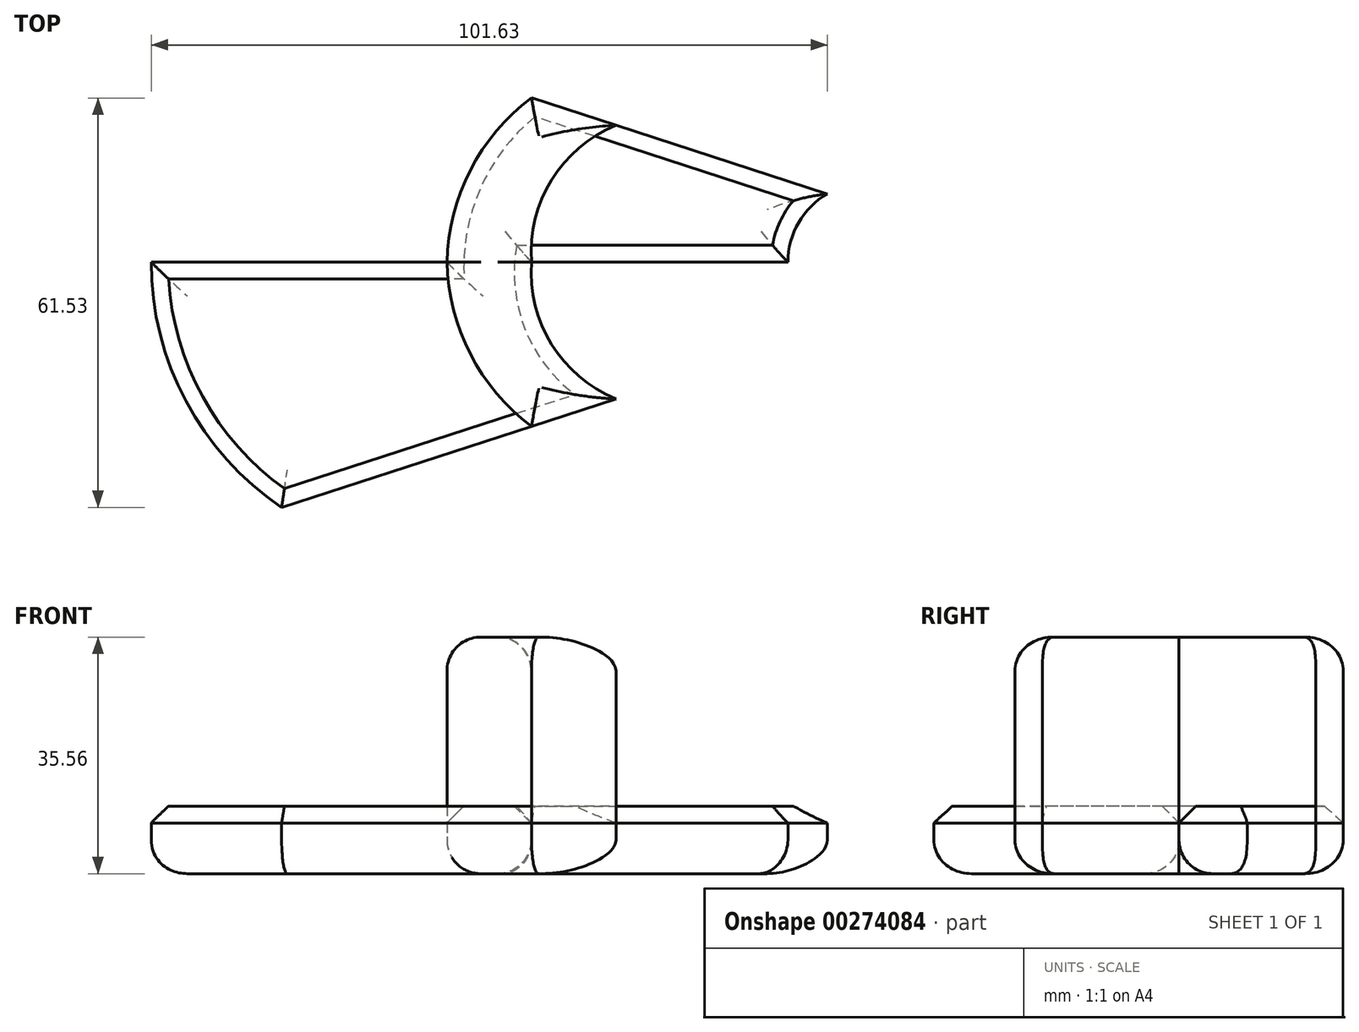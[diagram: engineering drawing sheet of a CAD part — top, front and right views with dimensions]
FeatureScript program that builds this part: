
annotation { "Feature Type Name" : "Feature", "Feature Type Description" : "" }
export const myFeature = defineFeature(function(context is Context, id is Id, definition is map)
    precondition{}
    {
        {
            var Q0;
            Q0=qCreatedBy(makeId("Top.planeOp"),FACE);
            var sketch = newSketch(context, id + "F0", { "sketchPlane" : qUnion([Q0])});
            skLineSegment(sketch, "E0", {"start": v(-50.8, 0) * mm, "end": v(-6.35, 0) * mm});
            skLineSegment(sketch, "E1.MirrorCS", {"start": v(50.8, 0) * mm, "end": v(6.37, 0) * mm});
            skArc(sketch, "E2", {"start": v(-50.8, 0) * mm, "mid": v(-45.6, 20.88) * mm, "end": v(-31.19, 36.86) * mm});
            skArc(sketch, "E3.MirrorCS", {"start": v(-50.8, 0) * mm, "mid": v(-45.6, -20.88) * mm, "end": v(-31.19, -36.86) * mm});
            skLineSegment(sketch, "E4", {"start": v(-31.19, 36.86) * mm, "end": v(50.83, 10.25) * mm});
            skLineSegment(sketch, "E5", {"start": v(50.83, -10.25) * mm, "end": v(-31.19, -36.86) * mm});
            skArc(sketch, "E6", {"start": v(50.83, 10.25) * mm, "mid": v(44.9, 0) * mm, "end": v(50.83, -10.25) * mm});
            skArc(sketch, "E7", {"start": v(6.37, 24.67) * mm, "mid": v(-2.83, 13.8) * mm, "end": v(-6.35, 0) * mm});
            skArc(sketch, "E8.MirrorCS", {"start": v(6.37, -24.67) * mm, "mid": v(-2.83, -13.8) * mm, "end": v(-6.35, 0) * mm});
            skLineSegment(sketch, "E9", {"start": v(6.37, 24.67) * mm, "end": v(19.07, 24.67) * mm});
            skArc(sketch, "E10", {"start": v(19.07, 20.55) * mm, "mid": v(9.36, 12.35) * mm, "end": v(6.37, 0) * mm});
            skArc(sketch, "E11.MirrorCS", {"start": v(19.07, -20.55) * mm, "mid": v(9.36, -12.35) * mm, "end": v(6.37, 0) * mm});
            skSolve(sketch);
        }
        {
            var Q0;
            {var subQ0=sQuery(id+"F0.wireOp",EDGE,"E10");Q0=makeQuery(id+"F0.imprint","IMPRINT",FACE,{"disambiguationData":[TD([[makeQuery(id+"F0.imprint","IMPRINT",EDGE,{"derivedFrom":subQ0}),1.0]])]});}
            var Q1;
            {var subQ0=sQuery(id+"F0.wireOp",EDGE,"E11.MirrorCS");Q1=makeQuery(id+"F0.imprint","IMPRINT",FACE,{"disambiguationData":[TD([[makeQuery(id+"F0.imprint","IMPRINT",EDGE,{"derivedFrom":subQ0}),-1.0]])]});}
            var Q2;
            {var subQ0=sQuery(id+"F0.wireOp",EDGE,"E2");Q2=makeQuery(id+"F0.imprint","IMPRINT",FACE,{"disambiguationData":[TD([[makeQuery(id+"F0.imprint","IMPRINT",EDGE,{"derivedFrom":subQ0}),-1.0]])]});}
            var Q3;
            Q3=makeQuery(id+"F0.imprint","IMPRINT",FACE,{"disambiguationData":[TD([[makeQuery(id+"F0.imprint","IMPRINT",EDGE,{"derivedFrom":sQuery(id+"F0.wireOp",EDGE,"E0")}),-1.0]])]});
            extrude(context, id + "F1", {"entities" : qUnion([Q0, Q1, Q2, Q3]), "depth" : 10.16 * mm});
        }
        {
            var Q0;
            {var subQ1=sQuery(id+"F0.wireOp",EDGE,"E7");Q0=makeQuery(id+"F0.imprint","IMPRINT",FACE,{"disambiguationData":[TD([[makeQuery(id+"F0.imprint","IMPRINT",EDGE,{"derivedFrom":subQ1}),1.0]])]});}
            extrude(context, id + "F2", {"entities" : qUnion([Q0]), "depth" : 35.56 * mm});
        }
        {
            var Q0;
            Q0=makeQuery(id+"F2.opExtrude","CAP_EDGE",EDGE,{"disambiguationData":[OSD([sQuery(id+"F0.wireOp",EDGE,"E11.MirrorCS")])],"isStart":false});
            var Q1;
            Q1=makeQuery(id+"F2.opExtrude","CAP_EDGE",EDGE,{"disambiguationData":[OSD([sQuery(id+"F0.wireOp",EDGE,"E10")])],"isStart":false});
            var Q2;
            Q2=makeQuery(id+"F2.opExtrude","CAP_FACE",FACE,{"disambiguationData":[OSD([sQuery(id+"F0.wireOp",EDGE,"E4"),sQuery(id+"F0.wireOp",EDGE,"E5"),sQuery(id+"F0.wireOp",EDGE,"E7"),sQuery(id+"F0.wireOp",EDGE,"E8.MirrorCS"),sQuery(id+"F0.wireOp",EDGE,"E10"),sQuery(id+"F0.wireOp",EDGE,"E11.MirrorCS")])],"isStart":false});
            fillet(context, id + "F3", {"entities" : qUnion([Q0, Q1, Q2]), "radius" : 5.08 * mm, "tangentPropagation" : true, "allowEdgeOverflow" : false});
        }
        {
            var Q0;
            Q0=makeQuery(id+"F1.opExtrude","CAP_FACE",FACE,{"disambiguationData":[OSD([sQuery(id+"F0.wireOp",EDGE,"E4"),sQuery(id+"F0.wireOp",EDGE,"E5"),sQuery(id+"F0.wireOp",EDGE,"E6"),sQuery(id+"F0.wireOp",EDGE,"E10"),sQuery(id+"F0.wireOp",EDGE,"E11.MirrorCS")])],"isStart":false});
            var Q1;
            Q1=makeQuery(id+"F1.opExtrude","CAP_FACE",FACE,{"disambiguationData":[OSD([sQuery(id+"F0.wireOp",EDGE,"E2"),sQuery(id+"F0.wireOp",EDGE,"E3.MirrorCS"),sQuery(id+"F0.wireOp",EDGE,"E4"),sQuery(id+"F0.wireOp",EDGE,"E5"),sQuery(id+"F0.wireOp",EDGE,"E7"),sQuery(id+"F0.wireOp",EDGE,"E8.MirrorCS")])],"isStart":false});
            var Q2;
            Q2=makeQuery(id+"F1.opExtrude","CAP_EDGE",EDGE,{"disambiguationData":[OSD([sQuery(id+"F0.wireOp",EDGE,"E8.MirrorCS")])],"isStart":false});
            var Q3;
            Q3=makeQuery(id+"F1.opExtrude","CAP_EDGE",EDGE,{"disambiguationData":[OSD([sQuery(id+"F0.wireOp",EDGE,"E7")])],"isStart":false});
            var Q4;
            Q4=makeQuery(id+"F1.opExtrude","CAP_EDGE",EDGE,{"disambiguationData":[OSD([sQuery(id+"F0.wireOp",EDGE,"E11.MirrorCS")])],"isStart":false});
            var Q5;
            Q5=makeQuery(id+"F1.opExtrude","CAP_EDGE",EDGE,{"disambiguationData":[OSD([sQuery(id+"F0.wireOp",EDGE,"E10")])],"isStart":false});
            chamfer(context, id + "F4", {"entities" : qUnion([Q0, Q1, Q2, Q3, Q4, Q5]), "width" : 2.54 * mm, "tangentPropagation" : true});
        }
        {
            var Q0;
            Q0=makeQuery(id+"F1.opExtrude","CAP_FACE",FACE,{"disambiguationData":[OSD([sQuery(id+"F0.wireOp",EDGE,"E4"),sQuery(id+"F0.wireOp",EDGE,"E5"),sQuery(id+"F0.wireOp",EDGE,"E6"),sQuery(id+"F0.wireOp",EDGE,"E10"),sQuery(id+"F0.wireOp",EDGE,"E11.MirrorCS")])],"isStart":true});
            var Q1;
            Q1=makeQuery(id+"F1.opExtrude","CAP_FACE",FACE,{"disambiguationData":[OSD([sQuery(id+"F0.wireOp",EDGE,"E2"),sQuery(id+"F0.wireOp",EDGE,"E3.MirrorCS"),sQuery(id+"F0.wireOp",EDGE,"E4"),sQuery(id+"F0.wireOp",EDGE,"E5"),sQuery(id+"F0.wireOp",EDGE,"E7"),sQuery(id+"F0.wireOp",EDGE,"E8.MirrorCS")])],"isStart":true});
            var Q2;
            Q2=makeQuery(id+"F2.opExtrude","CAP_FACE",FACE,{"disambiguationData":[OSD([sQuery(id+"F0.wireOp",EDGE,"E4"),sQuery(id+"F0.wireOp",EDGE,"E5"),sQuery(id+"F0.wireOp",EDGE,"E7"),sQuery(id+"F0.wireOp",EDGE,"E8.MirrorCS"),sQuery(id+"F0.wireOp",EDGE,"E10"),sQuery(id+"F0.wireOp",EDGE,"E11.MirrorCS")])],"isStart":true});
            fillet(context, id + "F5", {"entities" : qUnion([Q0, Q1, Q2]), "radius" : 5.08 * mm, "tangentPropagation" : true, "allowEdgeOverflow" : false});
        }
    });
